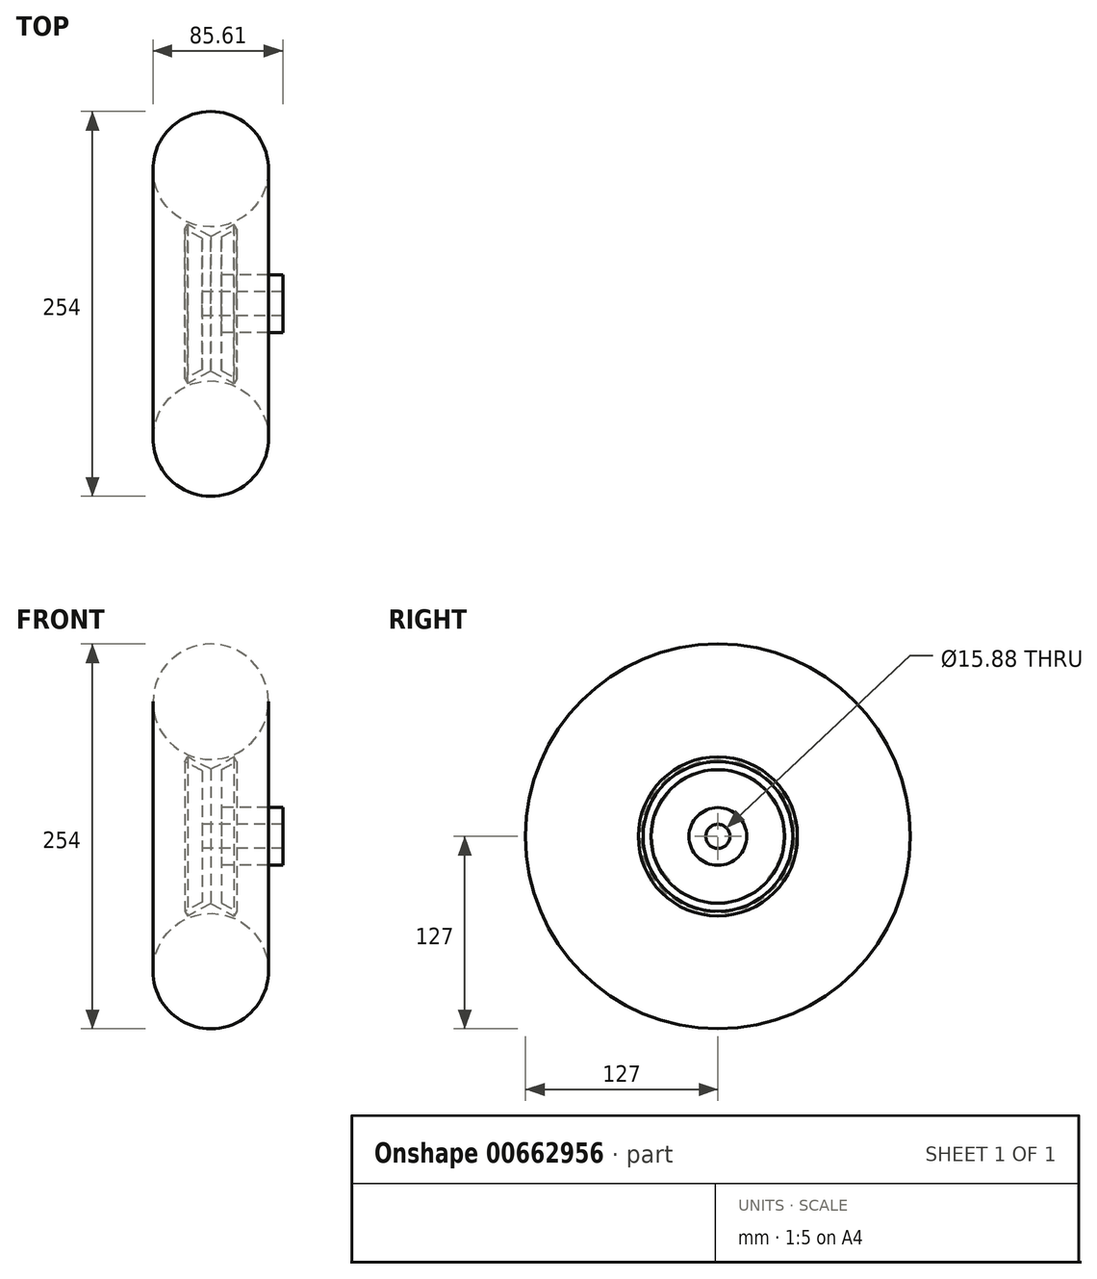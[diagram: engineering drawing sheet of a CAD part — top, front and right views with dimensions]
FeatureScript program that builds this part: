
annotation { "Feature Type Name" : "Feature", "Feature Type Description" : "" }
export const myFeature = defineFeature(function(context is Context, id is Id, definition is map)
    precondition{}
    {
        {
            var Q0;
            Q0=qCreatedBy(makeId("Front.planeOp"),FACE);
            var sketch = newSketch(context, id + "F0", { "sketchPlane" : qUnion([Q0])});
            skCircle(sketch, "E0", {"center": v(0, 88.9) * mm, "radius": 38.1 * mm});
            skLineSegment(sketch, "E1", {"start": v(-144.48, 0) * mm, "end": v(156.43, 0) * mm, "construction": true});
            skLineSegment(sketch, "E2", {"start": v(-5.65, 7.94) * mm, "end": v(-5.65, 43.36) * mm});
            skLineSegment(sketch, "E3", {"start": v(-5.65, 43.36) * mm, "end": v(-17.04, 49.36) * mm});
            skLineSegment(sketch, "E4", {"start": v(-17.04, 49.36) * mm, "end": v(-15.38, 52.5) * mm});
            skLineSegment(sketch, "E5", {"start": v(-15.38, 52.5) * mm, "end": v(0, 44.4) * mm});
            skLineSegment(sketch, "E6", {"start": v(0, 44.4) * mm, "end": v(15.38, 52.5) * mm});
            skLineSegment(sketch, "E7", {"start": v(15.38, 52.5) * mm, "end": v(17.04, 49.36) * mm});
            skLineSegment(sketch, "E8", {"start": v(17.04, 49.36) * mm, "end": v(7.05, 44.1) * mm});
            skLineSegment(sketch, "E9", {"start": v(7.05, 44.1) * mm, "end": v(7.05, 19.05) * mm});
            skLineSegment(sketch, "E10", {"start": v(7.05, 19.05) * mm, "end": v(47.5, 19.05) * mm});
            skLineSegment(sketch, "E11", {"start": v(47.5, 19.05) * mm, "end": v(47.5, 7.94) * mm});
            skLineSegment(sketch, "E12", {"start": v(-5.65, 7.94) * mm, "end": v(47.5, 7.94) * mm});
            skSolve(sketch);
        }
        {
            var Q0;
            Q0 = qSketchRegion(id + "F0", true);
            var Q1;
            Q1=sQuery(id+"F0.wireOp",EDGE,"E1");
            revolve(context, id + "F1", {"entities" : qUnion([Q0]), "axis" : qUnion([Q1]), "revolveType" : RevolveType.FULL});
        }
    });
